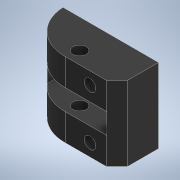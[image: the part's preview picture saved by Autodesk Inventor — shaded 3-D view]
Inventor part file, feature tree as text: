
AUTODESK INVENTOR PART (.ipt)
format: ipt  version: 2021 (Build 250183000, 183)  size: 148,992 bytes
history: native  units: mm
features: extrude x2, chamfer x2, sketch x2, fillet x1
ambient origin geometry x8: Origin, YZ Plane, XZ Plane, XY Plane, X Axis, Y Axis, Z Axis, Center Point
bodies: Solid1 (feature_tree)
feature tree (7):
  extrude  "Extrusion1"  Depth=6.0mm
  extrude  "Extrusion2"  Depth=18.0mm
  chamfer  "Chamfer1"  Distance=4.0mm
  chamfer  "Chamfer2"  Distance=2.8mm
  fillet  "Fillet1"  Radius=2.5mm
  sketch  "Sketch1"  dims[d0=6.0mm d1=6.0mm]
  sketch  "Sketch2"  dims[d2=5.0mm d3=18.0mm d5=4.0mm d6=2.8mm d7=2.5mm d8=2.5mm d9=18.0mm d10=10.0mm d11=0.0mm d12=3.0mm d13=3.2mm d14=11.0mm d15=0.0mm d16=0.0mm d17=6.0mm d18=2.0mm d19=45.0deg d20=2.5mm d21=2.0mm d22=45.0deg d23=10.5mm]
